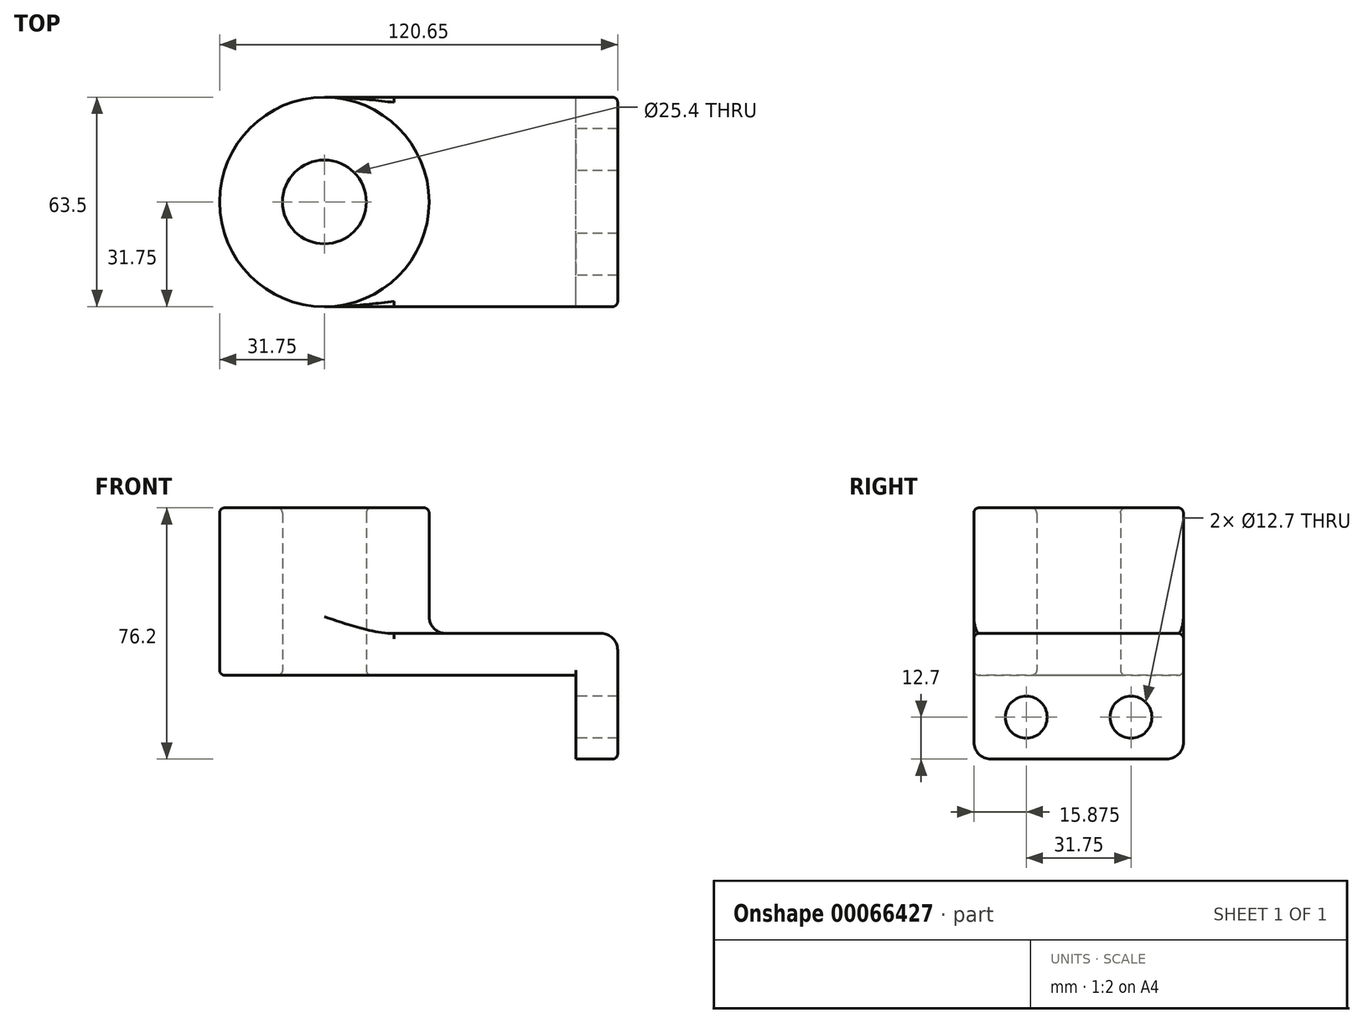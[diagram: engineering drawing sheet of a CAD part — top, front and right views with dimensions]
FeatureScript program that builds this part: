
annotation { "Feature Type Name" : "Feature", "Feature Type Description" : "" }
export const myFeature = defineFeature(function(context is Context, id is Id, definition is map)
    precondition{}
    {
        {
            var Q0;
            Q0=qCreatedBy(makeId("Top.planeOp"),FACE);
            var sketch = newSketch(context, id + "F0", { "sketchPlane" : qUnion([Q0])});
            skLineSegment(sketch, "E0.rect.bottom", {"start": v(38.1, -31.75) * mm, "end": v(-38.1, -31.75) * mm});
            skLineSegment(sketch, "E0.rect.top", {"start": v(38.1, 31.75) * mm, "end": v(-38.1, 31.75) * mm});
            skLineSegment(sketch, "E0.rect.left", {"start": v(38.1, -31.75) * mm, "end": v(38.1, 31.75) * mm});
            skLineSegment(sketch, "E0.rect.right", {"start": v(-38.1, -31.75) * mm, "end": v(-38.1, 31.75) * mm});
            skPoint(sketch, "E0.rect.middle", {"position": v(0, 0) * mm});
            skCircle(sketch, "E1", {"center": v(-38.1, 0) * mm, "radius": 31.75 * mm});
            skCircle(sketch, "E2", {"center": v(-38.1, 0) * mm, "radius": 12.7 * mm});
            skSolve(sketch);
        }
        {
            var Q0;
            {var subQ0=sQuery(id+"F0.wireOp",EDGE,"E0.rect.bottom");Q0=makeQuery(id+"F0.imprint","IMPRINT",FACE,{"disambiguationData":[TD([[makeQuery(id+"F0.imprint","IMPRINT",EDGE,{"derivedFrom":subQ0}),-1.0]])]});}
            var Q1;
            {var subQ1=sQuery(id+"F0.wireOp",EDGE,"E0.rect.right");var subQ3=sQuery(id+"F0.wireOp",EDGE,"E2");var subQ4=makeQuery(id+"F0.imprint","INTERSECT",VERTEX,{"disambiguationData":[OD(0.0)],"derivedFrom":[subQ1,subQ3]});Q1=makeQuery(id+"F0.imprint","IMPRINT",FACE,{"disambiguationData":[TD([[makeQuery(id+"F0.imprint","IMPRINT",EDGE,{"disambiguationData":[TD([[subQ4,-1.0]])],"derivedFrom":subQ3}),-1.0]])]});}
            var Q2;
            {var subQ1=sQuery(id+"F0.wireOp",EDGE,"E0.rect.right");var subQ3=sQuery(id+"F0.wireOp",EDGE,"E2");var subQ4=makeQuery(id+"F0.imprint","INTERSECT",VERTEX,{"disambiguationData":[OD(0.0)],"derivedFrom":[subQ1,subQ3]});Q2=makeQuery(id+"F0.imprint","IMPRINT",FACE,{"disambiguationData":[TD([[makeQuery(id+"F0.imprint","IMPRINT",EDGE,{"disambiguationData":[TD([[subQ4,1.0]])],"derivedFrom":subQ3}),-1.0]])]});}
            extrude(context, id + "F1", {"entities" : qUnion([Q0, Q1, Q2]), "depth" : 12.7 * mm});
        }
        {
            var Q0;
            {var subQ1=sQuery(id+"F0.wireOp",EDGE,"E0.rect.right");var subQ3=sQuery(id+"F0.wireOp",EDGE,"E2");var subQ4=makeQuery(id+"F0.imprint","INTERSECT",VERTEX,{"disambiguationData":[OD(0.0)],"derivedFrom":[subQ1,subQ3]});Q0=makeQuery(id+"F0.imprint","IMPRINT",FACE,{"disambiguationData":[TD([[makeQuery(id+"F0.imprint","IMPRINT",EDGE,{"disambiguationData":[TD([[subQ4,-1.0]])],"derivedFrom":subQ3}),-1.0]])]});}
            var Q1;
            {var subQ1=sQuery(id+"F0.wireOp",EDGE,"E0.rect.right");var subQ3=sQuery(id+"F0.wireOp",EDGE,"E2");var subQ4=makeQuery(id+"F0.imprint","INTERSECT",VERTEX,{"disambiguationData":[OD(0.0)],"derivedFrom":[subQ1,subQ3]});Q1=makeQuery(id+"F0.imprint","IMPRINT",FACE,{"disambiguationData":[TD([[makeQuery(id+"F0.imprint","IMPRINT",EDGE,{"disambiguationData":[TD([[subQ4,1.0]])],"derivedFrom":subQ3}),-1.0]])]});}
            extrude(context, id + "F2", {"entities" : qUnion([Q0, Q1]), "operationType" : NewBodyOperationType.ADD, "depth" : 50.8 * mm});
        }
        {
            var Q0;
            Q0=makeQuery(id+"F1.opExtrude","SWEPT_FACE",FACE,{"disambiguationData":[OSD([sQuery(id+"F0.wireOp",EDGE,"E0.rect.left")])]});
            var sketch = newSketch(context, id + "F3", { "sketchPlane" : qUnion([Q0])});
            skLineSegment(sketch, "E3.bottom", {"start": v(-31.75, 12.7) * mm, "end": v(31.75, 12.7) * mm});
            skLineSegment(sketch, "E3.top", {"start": v(-31.75, -25.4) * mm, "end": v(31.75, -25.4) * mm});
            skLineSegment(sketch, "E3.left", {"start": v(-31.75, 12.7) * mm, "end": v(-31.75, -25.4) * mm});
            skLineSegment(sketch, "E3.right", {"start": v(31.75, 12.7) * mm, "end": v(31.75, -25.4) * mm});
            skLineSegment(sketch, "E4", {"start": v(0, 0) * mm, "end": v(0, -25.4) * mm, "construction": true});
            skCircle(sketch, "E5", {"center": v(-15.87, -12.7) * mm, "radius": 6.35 * mm});
            skCircle(sketch, "E6.MirrorC", {"center": v(15.88, -12.7) * mm, "radius": 6.35 * mm});
            skSolve(sketch);
        }
        {
            var Q0;
            Q0 = qSketchRegion(id + "F3", true);
            extrude(context, id + "F4", {"entities" : qUnion([Q0]), "operationType" : NewBodyOperationType.ADD, "depth" : 12.7 * mm});
        }
        {
            var Q0;
            {var subQ0=sQuery(id+"F0.wireOp",EDGE,"E1");Q0=makeQuery(id+"F2.boolean.opBoolean","INTERSECT",EDGE,{"derivedFrom":[makeQuery(id+"F1.opExtrude","CAP_FACE",FACE,{"disambiguationData":[OSD([sQuery(id+"F0.wireOp",EDGE,"E0.rect.bottom"),sQuery(id+"F0.wireOp",EDGE,"E0.rect.top"),sQuery(id+"F0.wireOp",EDGE,"E0.rect.left"),subQ0,sQuery(id+"F0.wireOp",EDGE,"E2")])],"isStart":false}),makeQuery(id+"F2.opExtrude","SWEPT_FACE",FACE,{"disambiguationData":[OSD([subQ0])]})]});}
            var Q1;
            Q1=makeQuery(id+"F4.opExtrude","CAP_EDGE",EDGE,{"disambiguationData":[OSD([sQuery(id+"F3.wireOp",EDGE,"E3.bottom")])],"isStart":false});
            var Q2;
            Q2=makeQuery(id+"F4.opExtrude","SWEPT_EDGE",EDGE,{"disambiguationData":[OSD([sQuery(id+"F3.wireOp",EDGE,"E3.top"),sQuery(id+"F3.wireOp",EDGE,"E3.left")])]});
            var Q3;
            Q3=makeQuery(id+"F4.opExtrude","SWEPT_EDGE",EDGE,{"disambiguationData":[OSD([sQuery(id+"F3.wireOp",EDGE,"E3.top"),sQuery(id+"F3.wireOp",EDGE,"E3.right")])]});
            var Q4;
            Q4=makeQuery(id+"F1.opExtrude","CAP_EDGE",EDGE,{"disambiguationData":[OSD([sQuery(id+"F0.wireOp",EDGE,"E0.rect.left")])],"isStart":true});
            fillet(context, id + "F5", {"entities" : qUnion([Q0, Q1, Q2, Q3, Q4]), "radius" : 5.08 * mm, "tangentPropagation" : true, "allowEdgeOverflow" : false});
        }
        {
            var Q0;
            Q0=makeQuery(id+"F4.boolean.opBoolean","MERGE",EDGE,{"derivedFrom":[makeQuery(id+"F1.opExtrude","CAP_EDGE",EDGE,{"disambiguationData":[OSD([sQuery(id+"F0.wireOp",EDGE,"E0.rect.bottom")])],"isStart":false}),makeQuery(id+"F4.opExtrude","SWEPT_EDGE",EDGE,{"disambiguationData":[OSD([sQuery(id+"F3.wireOp",EDGE,"E3.bottom"),sQuery(id+"F3.wireOp",EDGE,"E3.left")])]})]});
            var Q1;
            Q1=makeQuery(id+"F2.opExtrude","CAP_EDGE",EDGE,{"disambiguationData":[OSD([sQuery(id+"F0.wireOp",EDGE,"E2")])],"isStart":false});
            var Q2;
            Q2=makeQuery(id+"F2.opExtrude","CAP_EDGE",EDGE,{"disambiguationData":[OSD([sQuery(id+"F0.wireOp",EDGE,"E1")])],"isStart":false});
            var Q3;
            Q3=makeQuery(id+"F1.opExtrude","CAP_EDGE",EDGE,{"disambiguationData":[OSD([sQuery(id+"F0.wireOp",EDGE,"E0.rect.top")])],"isStart":true});
            var Q4;
            Q4=makeQuery(id+"F1.opExtrude","CAP_EDGE",EDGE,{"disambiguationData":[OSD([sQuery(id+"F0.wireOp",EDGE,"E2")])],"isStart":true});
            fillet(context, id + "F6", {"entities" : qUnion([Q0, Q1, Q2, Q3, Q4]), "radius" : 1.59 * mm, "tangentPropagation" : true, "allowEdgeOverflow" : false});
        }
    });
